# Revit family: TemID_UHF считыватель дальнего действия до 8 метров_UHF 5E Lite
name_source: partatom
category: Охранная сигнализация
units: mm (PartAtom-declared; Revit-internal decimal feet)

## family parameters
Всегда вертикально = Нет
На основе рабочей плоскости = Нет
Общий = Да
При загрузке вырезать с полостями = Нет
Размер круглого соединителя = Использовать диаметр
Сохранять ориентацию аннотаций = Нет
Тип детали = Нормальный
Точка расчета площади = Да

## types (1)
- UHF 5E Lite
    =Габариты= = =Габариты=
    ADSK_Единица измерения = шт.
    ADSK_Завод-изготовитель = Temid
    ADSK_Количество = 1
    ADSK_Марка = UHF 5E Lite
    ADSK_Наименование = UHF считыватель дальнего действия до 8 метров
    ADSK_Обозначение = RD
    ADSK_Раздел спецификации = 3. Периферийное оборудование
    ADSK_Размер_Высота = 240 мм
    ADSK_Размер_Глубина = 63 мм
    ADSK_Размер_Ширина = 240 мм
    ADSK_Тип = UHF 5E Lite
    URL = https://temid-global.ru
    Зона обслуживания_Отступ от прибора = 50 мм
    Материал = Белый
    Отметка по умолчанию = 0 мм
    УГО_Тип = УГО_СКУД_Считыватель
